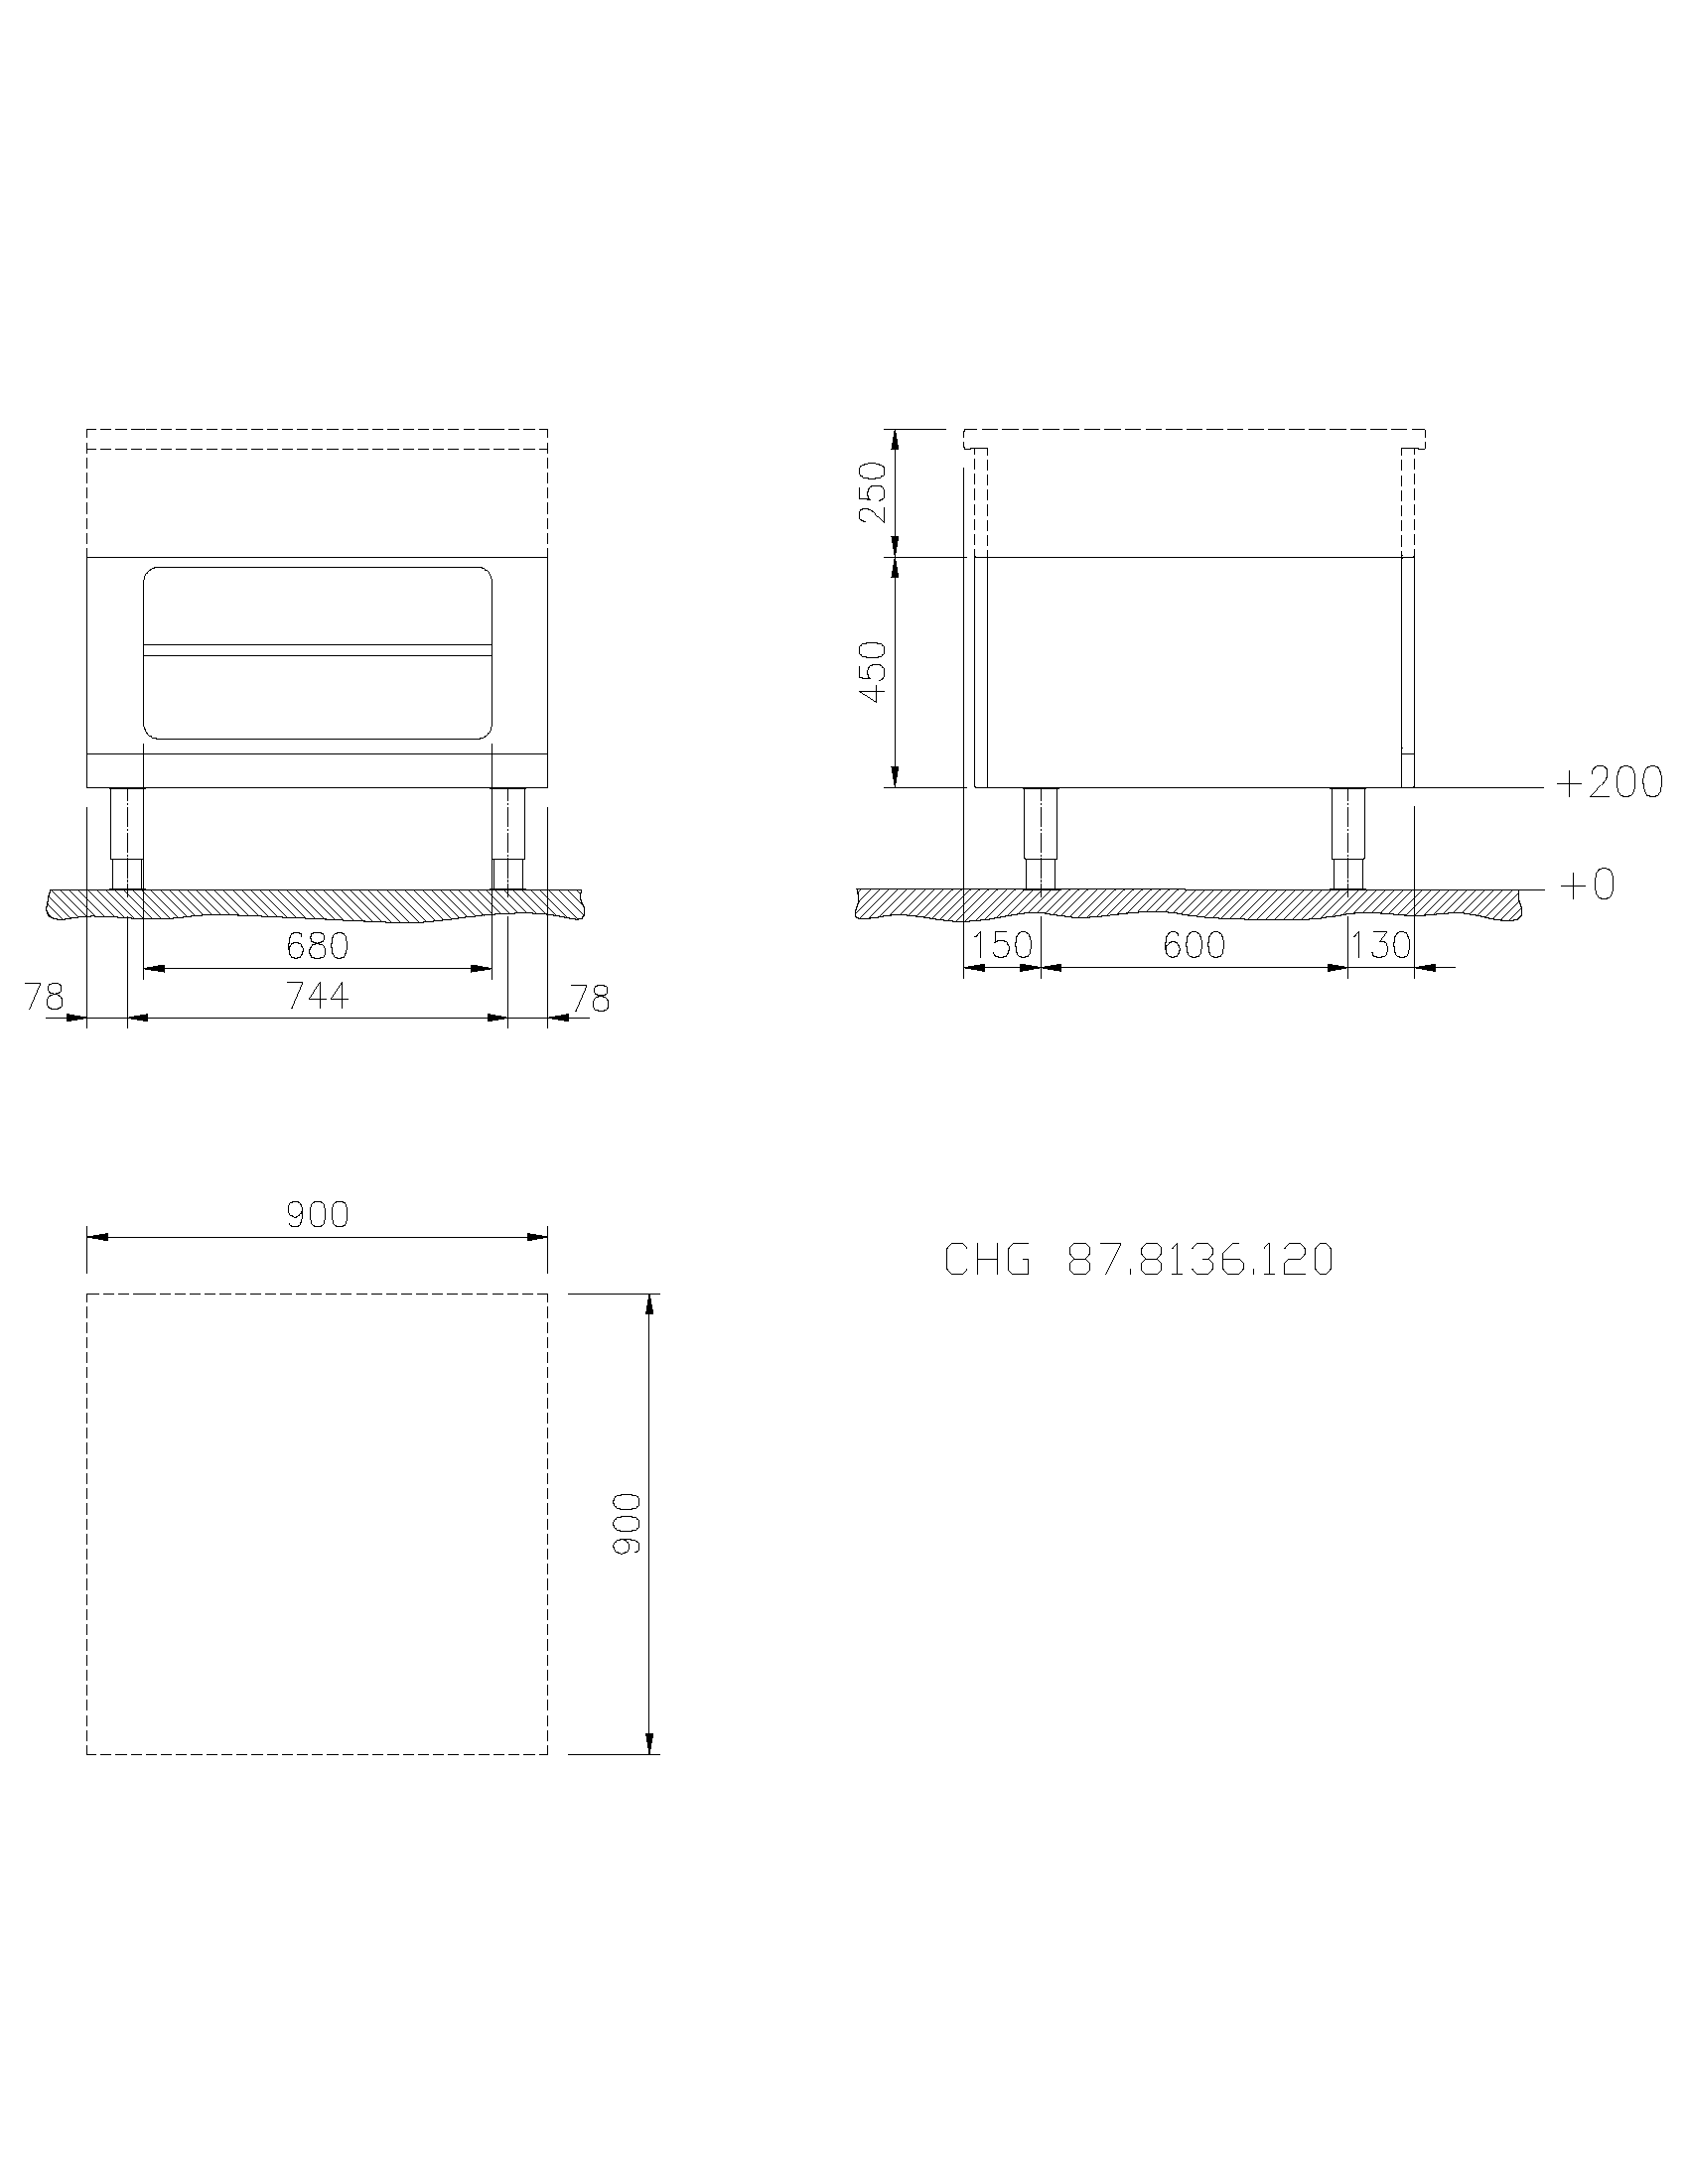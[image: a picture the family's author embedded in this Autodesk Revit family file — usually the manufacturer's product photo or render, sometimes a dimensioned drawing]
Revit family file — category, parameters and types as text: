
# Revit family: QF_ELECTROLUXPROFESSIONAL_589808_MC1HCAHOOM
name_source: partatom
category: Attrezzature speciali
units: mm (PartAtom-declared; Revit-internal decimal feet)

## family parameters
Basato su piano di lavoro = No
Condiviso = No
Punto di calcolo locali = No
Quota connettore circolare = Usa diametro
Sempre verticale = Sì
Taglio con vuoti quando caricato = No
Tipo di parte = Normale

## types (1)
- Standard
    Accessory = Sì
    Cold Water Size = 0"
    Compressed Air Pressure = 0.00 psi
    Compressed Air Size = 0"
    Compressed Air Volume = 0 GPM
    Condensate Return Size = 0"
    Cycle = 0 Hz
    Depth Actual = 900 mm  [stored 2.95276 ft]
    Descrizione = OPEN BASE,H3,GN,1S,800X900X450 MARINE
    Direct Waste Size = 0"
    Gas Input Pressure = 0.0
    Gas KW = 0
    Gas Size = 0"
    HP = 0 HP
    Height Actual = 450 mm  [stored 1.47638 ft]
    Hot Water Size = 0"
    Item Number = 589808
    Length Actual = 800 mm  [stored 2.62467 ft]
    Modello = MC1HCAHOOM
    Phase = 0
    Produttore = Electrolux Professional
    Prospetto di default = 0 mm  [stored 0 ft]
    Refrigerant Compressor Remote = Sì
    Refrigeration Liquid Line Size = 0 mm  [stored 0 ft]
    Refrigeration Suction Line Size = 0 mm  [stored 0 ft]
    Steam Consumption per Hour = 0
    Steam Supply Maximum Pressure = 0.00 psi
    Steam Supply Minimum Pressure = 0.00 psi
    Steam Supply Size = 0"
    URL = https://www.electroluxprofessional.com
    URL Manufacturer = https://www.electroluxprofessional.com
    Volts = 0 V
    Watts = 0 W
    Weight = 22.00 kg

note: source unit labels omitted for Gas Input Pressure — the stored unit's dimension contradicts the parameter name (converter mislabeling)

note: [stored X ft] marks values corroborated as IEEE doubles in the binary element streams (Revit-internal decimal feet)

## geometry (parser evidence)
native form markers: Blend x10, Sweep x2
no freeform markers — native parametric forms only
